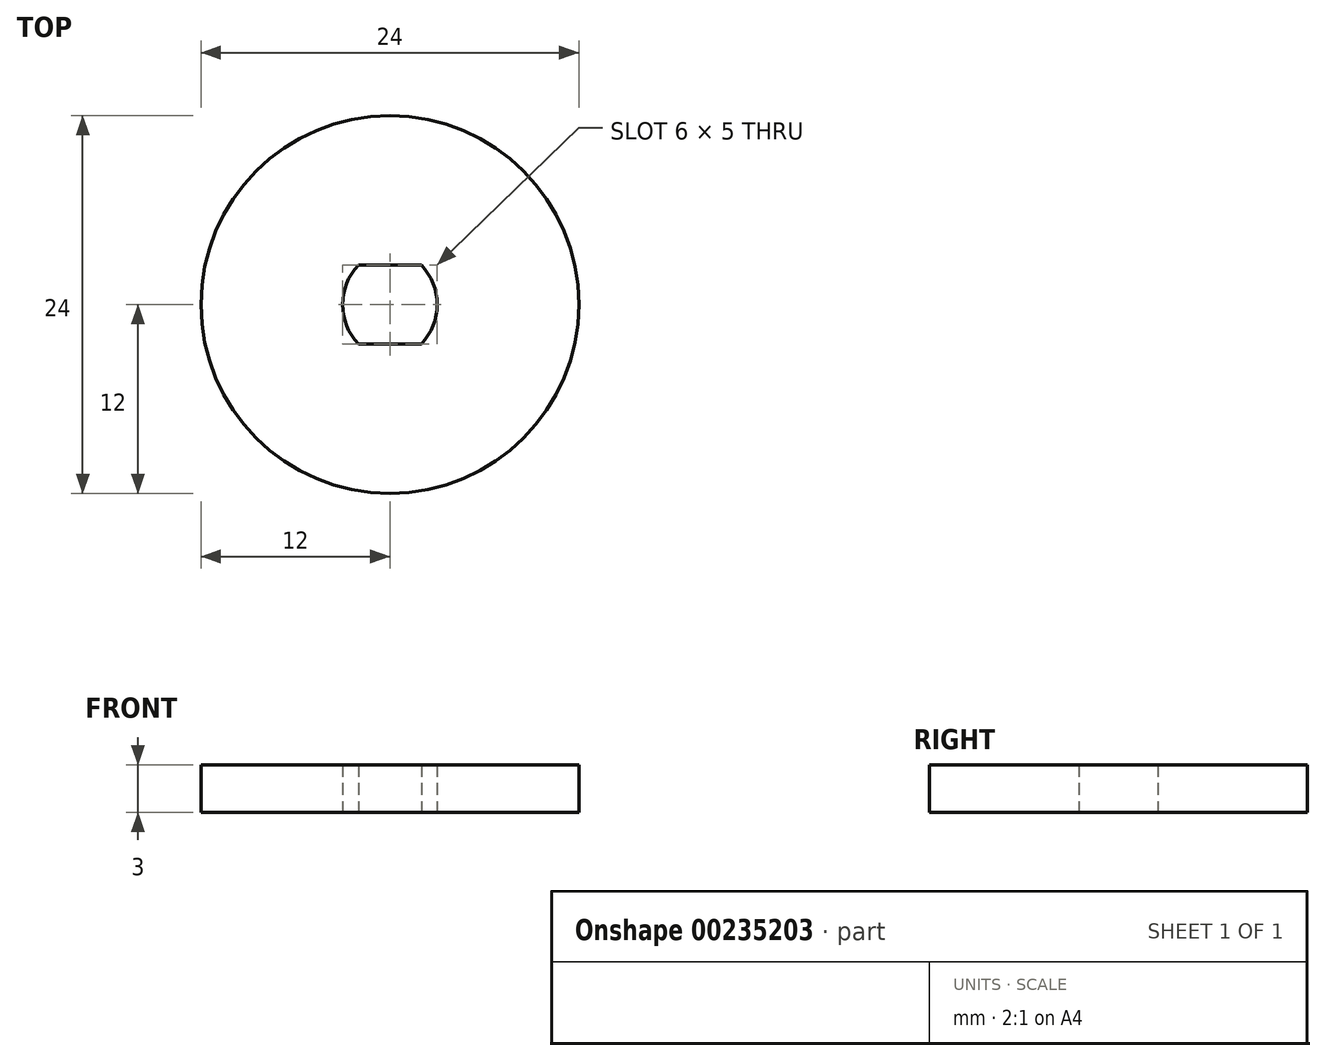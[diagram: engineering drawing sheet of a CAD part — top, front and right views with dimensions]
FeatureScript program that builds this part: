
annotation { "Feature Type Name" : "Feature", "Feature Type Description" : "" }
export const myFeature = defineFeature(function(context is Context, id is Id, definition is map)
    precondition{}
    {
        {
            var Q0;
            Q0=qCreatedBy(makeId("Top.planeOp"),FACE);
            var sketch = newSketch(context, id + "F0", { "sketchPlane" : qUnion([Q0])});
            skLineSegment(sketch, "E0.bottom", {"start": v(0, 0) * mm, "end": v(4, 0) * mm});
            skLineSegment(sketch, "E0.top", {"start": v(0, -5) * mm, "end": v(4, -5) * mm});
            skLineSegment(sketch, "E0.left", {"start": v(0, 0) * mm, "end": v(0, -5) * mm, "construction": true});
            skLineSegment(sketch, "E0.right", {"start": v(4, 0) * mm, "end": v(4, -5) * mm, "construction": true});
            skLineSegment(sketch, "E1", {"start": v(-1, -2.5) * mm, "end": v(5, -2.5) * mm, "construction": true});
            skPoint(sketch, "E1.startSnap0", {"position": v(0, -2.5) * mm});
            skArc(sketch, "E2", {"start": v(0, 0) * mm, "mid": v(-1, -2.5) * mm, "end": v(0, -5) * mm});
            skArc(sketch, "E3", {"start": v(4, -5) * mm, "mid": v(5, -2.5) * mm, "end": v(4, 0) * mm});
            skCircle(sketch, "E4", {"center": v(2, -2.5) * mm, "radius": 12 * mm});
            skSolve(sketch);
        }
        {
            var Q0;
            Q0=makeQuery(id+"F0.imprint","IMPRINT",FACE,{"disambiguationData":[TD([[makeQuery(id+"F0.imprint","IMPRINT",EDGE,{"derivedFrom":sQuery(id+"F0.wireOp",EDGE,"E0.bottom")}),1.0]])]});
            extrude(context, id + "F1", {"entities" : qUnion([Q0]), "depth" : 3 * mm, "offsetDistance" : 25 * mm});
        }
    });
